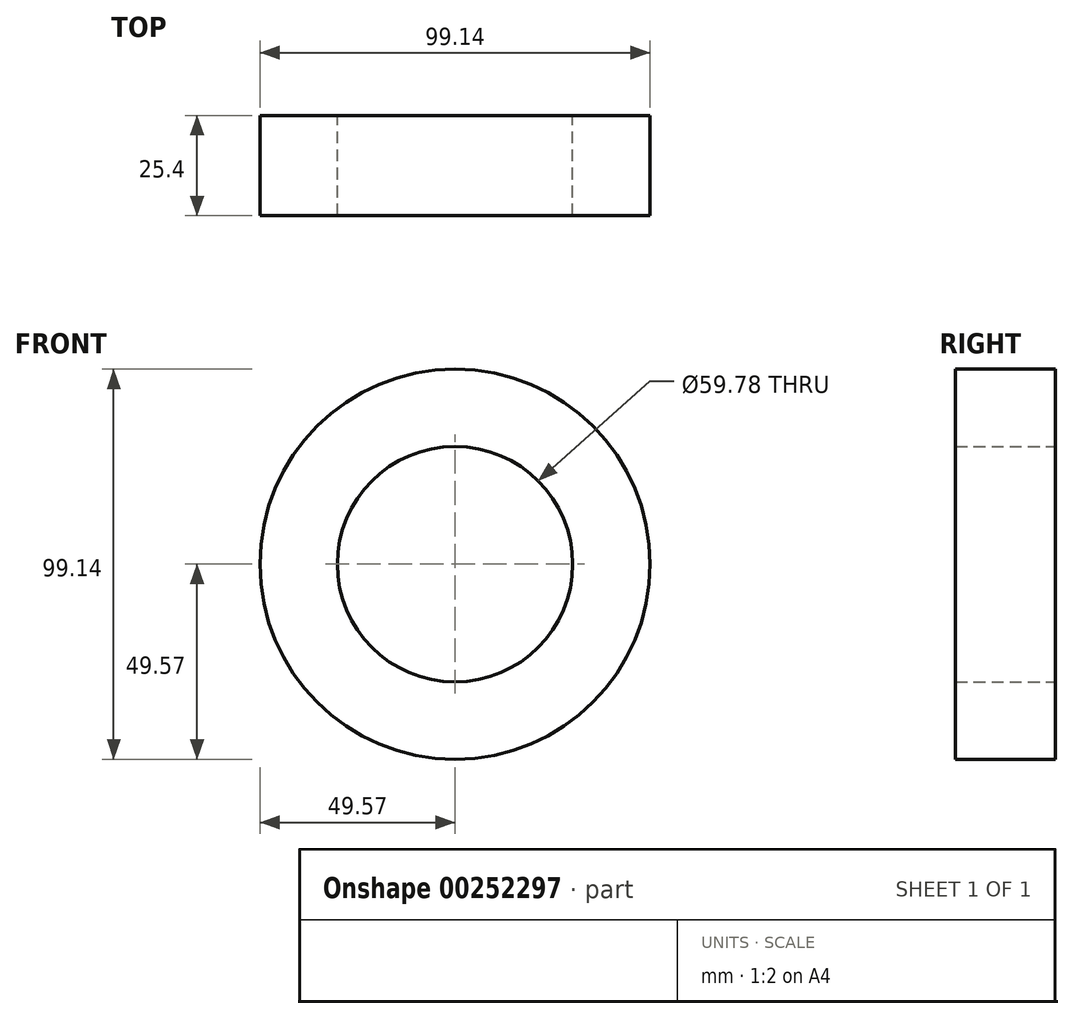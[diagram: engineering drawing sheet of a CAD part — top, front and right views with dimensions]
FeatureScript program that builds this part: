
annotation { "Feature Type Name" : "Feature", "Feature Type Description" : "" }
export const myFeature = defineFeature(function(context is Context, id is Id, definition is map)
    precondition{}
    {
        {
            var Q0;
            Q0=qCreatedBy(makeId("Front.planeOp"),FACE);
            var sketch = newSketch(context, id + "F0", { "sketchPlane" : qUnion([Q0])});
            skCircle(sketch, "E0", {"center": v(0, 0) * mm, "radius": 49.57 * mm});
            skCircle(sketch, "E1", {"center": v(0, 0) * mm, "radius": 29.9 * mm});
            skSolve(sketch);
        }
        {
            var Q0;
            Q0=makeQuery(id+"F0.imprint","IMPRINT",FACE,{"disambiguationData":[TD([[makeQuery(id+"F0.imprint","IMPRINT",EDGE,{"derivedFrom":sQuery(id+"F0.wireOp",EDGE,"E0")}),1.0]])]});
            extrude(context, id + "F1", {"entities" : qUnion([Q0]), "depth" : 25.4 * mm});
        }
    });
